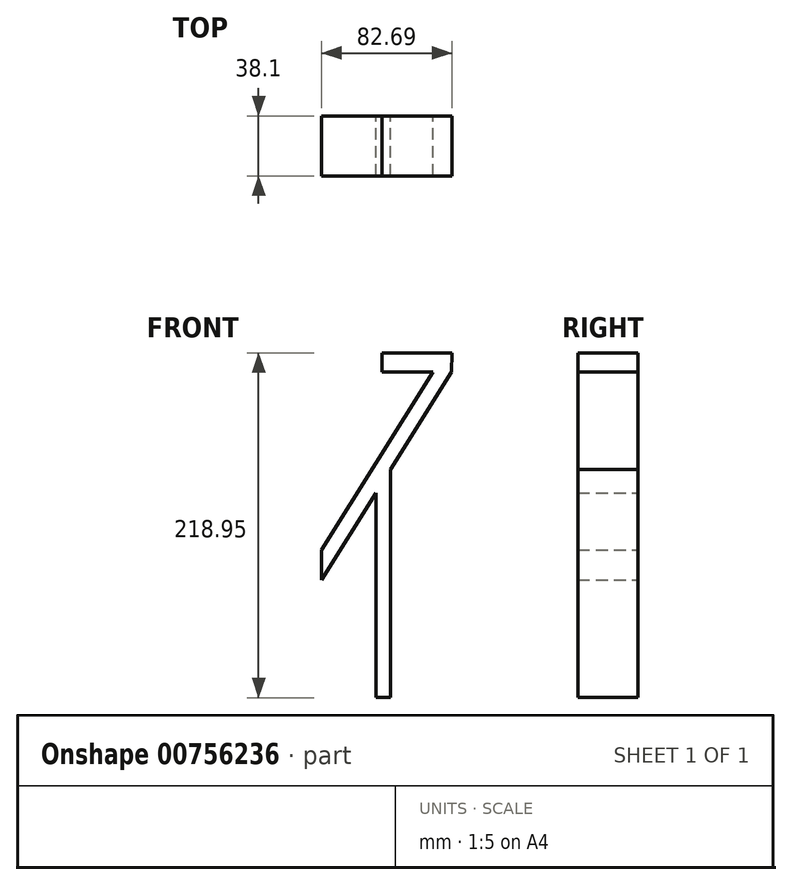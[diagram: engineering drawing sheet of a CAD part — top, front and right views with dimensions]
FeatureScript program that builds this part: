
annotation { "Feature Type Name" : "Feature", "Feature Type Description" : "" }
export const myFeature = defineFeature(function(context is Context, id is Id, definition is map)
    precondition{}
    {
        {
            var Q0;
            Q0=qCreatedBy(makeId("Front.planeOp"),FACE);
            var sketch = newSketch(context, id + "F0", { "sketchPlane" : qUnion([Q0])});
            skLineSegment(sketch, "E0", {"start": v(0, 59.47) * mm, "end": v(0, -85.76) * mm});
            skLineSegment(sketch, "E1", {"start": v(-43.72, -10.88) * mm, "end": v(38.85, 121.25) * mm});
            skLineSegment(sketch, "E2", {"start": v(38.85, 121.25) * mm, "end": v(-5.39, 121.25) * mm});
            skLineSegment(sketch, "E3", {"start": v(-9.17, 44.4) * mm, "end": v(-9.17, -85.62) * mm});
            skLineSegment(sketch, "E4", {"start": v(-9.17, -85.62) * mm, "end": v(0, -85.76) * mm});
            skLineSegment(sketch, "E5", {"start": v(-43.72, -10.88) * mm, "end": v(-43.72, 8.05) * mm});
            skLineSegment(sketch, "E6", {"start": v(-43.72, 8.05) * mm, "end": v(27.02, 121.25) * mm});
            skLineSegment(sketch, "E7", {"start": v(-5.39, 121.25) * mm, "end": v(-5.39, 133.2) * mm});
            skLineSegment(sketch, "E8", {"start": v(-5.39, 133.2) * mm, "end": v(38.97, 133.2) * mm});
            skLineSegment(sketch, "E9", {"start": v(38.97, 133.2) * mm, "end": v(38.85, 121.25) * mm});
            skSolve(sketch);
        }
        {
            var Q0;
            {var subQ0=sQuery(id+"F0.wireOp",EDGE,"E7");Q0=makeQuery(id+"F0.imprint","IMPRINT",FACE,{"disambiguationData":[TD([[makeQuery(id+"F0.imprint","IMPRINT",EDGE,{"derivedFrom":subQ0}),-1.0]])]});}
            var Q1;
            {var subQ6=sQuery(id+"F0.wireOp",EDGE,"E5");Q1=makeQuery(id+"F0.imprint","IMPRINT",FACE,{"disambiguationData":[TD([[makeQuery(id+"F0.imprint","IMPRINT",EDGE,{"derivedFrom":subQ6}),-1.0]])]});}
            var Q2;
            {var subQ4=sQuery(id+"F0.wireOp",EDGE,"E3");Q2=makeQuery(id+"F0.imprint","IMPRINT",FACE,{"disambiguationData":[TD([[makeQuery(id+"F0.imprint","IMPRINT",EDGE,{"derivedFrom":subQ4}),1.0]])]});}
            extrude(context, id + "F1", {"entities" : qUnion([Q0, Q1, Q2]), "endBound" : BoundingType.SYMMETRIC, "depth" : 38.1 * mm, "offsetDistance" : 25.4 * mm});
        }
    });
